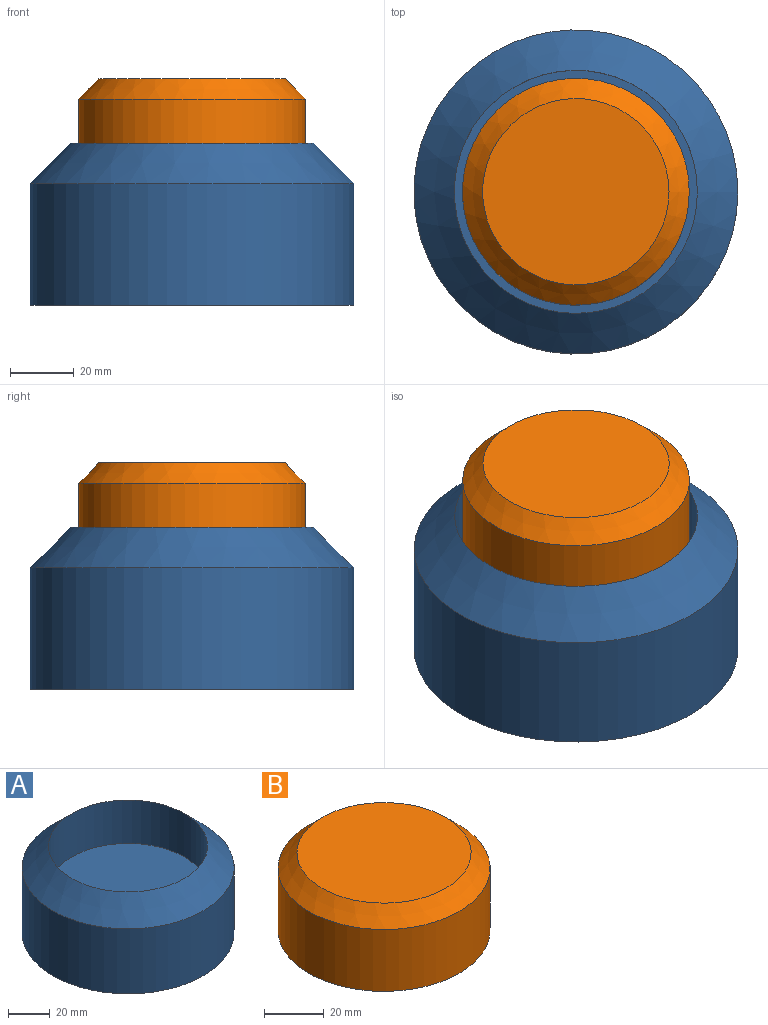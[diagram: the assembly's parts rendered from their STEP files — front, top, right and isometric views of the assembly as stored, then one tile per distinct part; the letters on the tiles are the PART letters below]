
ASSEMBLY  parts=2 mates=1
PART A: 7 faces, bbox 101.6x101.6x50.8 mm
  f0: cylinder r=50.8mm len=101.6mm, axis (0,0,-1), area 12161mm2, adj f1,f2
  f1: plane 101.6x101.6mm, normal (0,0,-1), area 1900.2mm2, adj f0,f5
  f2: cone r=38.1mm half-angle=45deg, axis (0,0,-1), area 5016.1mm2, adj f0,f3
  f3: cylinder r=38.1mm len=76.2mm, axis (0,0,1), area 6080.5mm2, adj f2,f4
  f4: plane 76.2x76.2mm, normal (0,0,1), area 4560.4mm2, adj f3
  f5: cylinder r=44.45mm len=88.9mm, axis (0,0,-1), area 5320.4mm2, adj f1,f6
  f6: plane 88.9x88.9mm, normal (0,0,-1), area 6207.2mm2, adj f5
PART B: 4 faces, bbox 71.1x71.1x31.8 mm
  f0: cylinder r=35.56mm len=71.12mm, axis (0,0,-1), area 5675.1mm2, adj f2,f3
  f1: plane 58.42x58.42mm, normal (0,0,1), area 2680.5mm2, adj f3
  f2: plane 71.12x71.12mm, normal (0,0,-1), area 3972.6mm2, adj f0
  f3: cone r=29.21mm half-angle=45deg, axis (0,0,-1), area 1827.3mm2, adj f0,f1
PLACE A at identity
PLACE B t=(0,0,39.19)mm
MATE slider B.f0 <-> A.f0  axis (0,0,-1) through (0,0,39.19)mm
